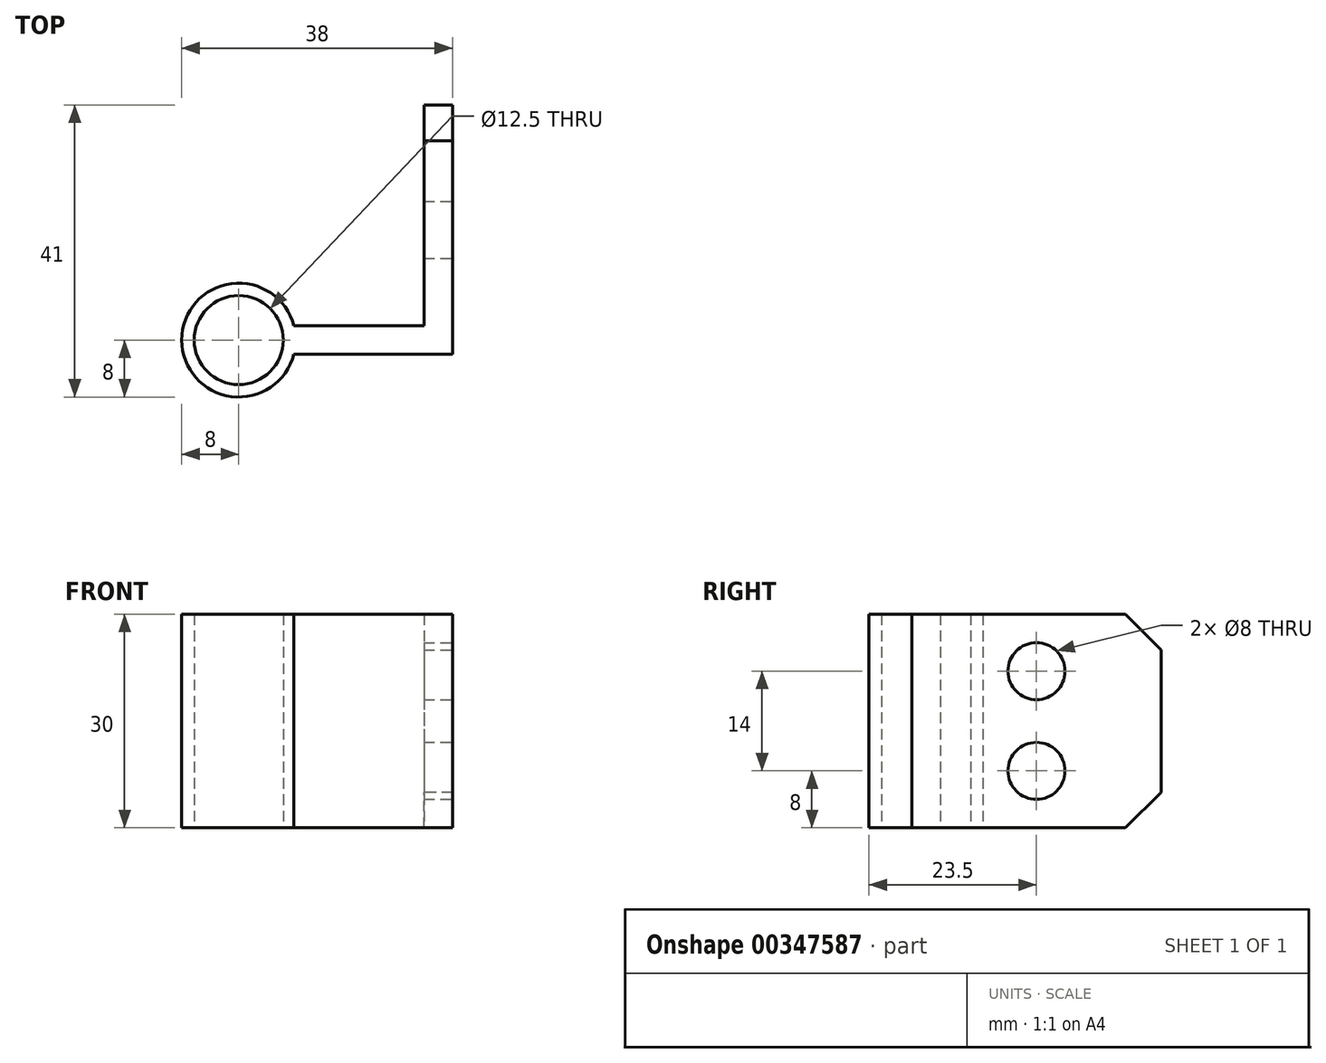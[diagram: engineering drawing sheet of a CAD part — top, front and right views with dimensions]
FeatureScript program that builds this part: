
annotation { "Feature Type Name" : "Feature", "Feature Type Description" : "" }
export const myFeature = defineFeature(function(context is Context, id is Id, definition is map)
    precondition{}
    {
        {
            var Q0;
            Q0=qCreatedBy(makeId("Top.planeOp"),FACE);
            var sketch = newSketch(context, id + "F0", { "sketchPlane" : qUnion([Q0])});
            skCircle(sketch, "E0", {"center": v(0, 0) * mm, "radius": 6.25 * mm});
            skArc(sketch, "E1", {"start": v(7.75, 2) * mm, "mid": v(-8, 0) * mm, "end": v(7.75, -2) * mm});
            skLineSegment(sketch, "E2.bottom", {"start": v(7.75, 2) * mm, "end": v(26, 2) * mm});
            skLineSegment(sketch, "E2.top", {"start": v(7.75, -2) * mm, "end": v(30, -2) * mm});
            skLineSegment(sketch, "E2.right", {"start": v(30, 2) * mm, "end": v(30, -2) * mm});
            skLineSegment(sketch, "E3.bottom", {"start": v(30, -2) * mm, "end": v(26, -2) * mm});
            skLineSegment(sketch, "E3.top", {"start": v(30, 33) * mm, "end": v(26, 33) * mm});
            skLineSegment(sketch, "E3.left", {"start": v(30, -2) * mm, "end": v(30, 33) * mm});
            skLineSegment(sketch, "E3.right", {"start": v(26, 2) * mm, "end": v(26, 33) * mm});
            skSolve(sketch);
        }
        {
            var Q0;
            Q0=makeQuery(id+"F0.imprint","IMPRINT",FACE,{"disambiguationData":[TD([[makeQuery(id+"F0.imprint","IMPRINT",EDGE,{"derivedFrom":sQuery(id+"F0.wireOp",EDGE,"E0")}),-1.0]])]});
            extrude(context, id + "F1", {"entities" : qUnion([Q0]), "depth" : 30 * mm});
        }
        {
            var Q0;
            Q0=makeQuery(id+"F1.opExtrude","SWEPT_FACE",FACE,{"disambiguationData":[OSD([sQuery(id+"F0.wireOp",EDGE,"E3.left")])]});
            var sketch = newSketch(context, id + "F2", { "sketchPlane" : qUnion([Q0])});
            skLineSegment(sketch, "E4", {"start": v(15.5, 30) * mm, "end": v(15.5, 0) * mm, "construction": true});
            skLineSegment(sketch, "E5", {"start": v(5.88, 22) * mm, "end": v(21.73, 22) * mm, "construction": true});
            skLineSegment(sketch, "E6", {"start": v(20.7, 8) * mm, "end": v(9.86, 8) * mm, "construction": true});
            skCircle(sketch, "E7", {"center": v(15.5, 22) * mm, "radius": 4 * mm});
            skCircle(sketch, "E8", {"center": v(15.5, 8) * mm, "radius": 4 * mm});
            skSolve(sketch);
        }
        {
            var Q0;
            Q0=makeQuery(id+"F2.imprint","IMPRINT",FACE,{"disambiguationData":[TD([[makeQuery(id+"F2.imprint","IMPRINT",EDGE,{"derivedFrom":sQuery(id+"F2.wireOp",EDGE,"E7")}),1.0]])]});
            var Q1;
            Q1=makeQuery(id+"F2.imprint","IMPRINT",FACE,{"disambiguationData":[TD([[makeQuery(id+"F2.imprint","IMPRINT",EDGE,{"derivedFrom":sQuery(id+"F2.wireOp",EDGE,"E8")}),1.0]])]});
            extrude(context, id + "F3", {"entities" : qUnion([Q0, Q1]), "operationType" : NewBodyOperationType.REMOVE, "endBound" : BoundingType.THROUGH_ALL, "oppositeDirection" : true, "depth" : 25 * mm});
        }
        {
            var Q0;
            Q0=makeQuery(id+"F1.opExtrude","CAP_EDGE",EDGE,{"disambiguationData":[OSD([sQuery(id+"F0.wireOp",EDGE,"E3.top")])],"isStart":false});
            var Q1;
            Q1=makeQuery(id+"F1.opExtrude","CAP_EDGE",EDGE,{"disambiguationData":[OSD([sQuery(id+"F0.wireOp",EDGE,"E3.top")])],"isStart":true});
            chamfer(context, id + "F4", {"entities" : qUnion([Q0, Q1]), "width" : 5 * mm, "tangentPropagation" : true});
        }
    });
